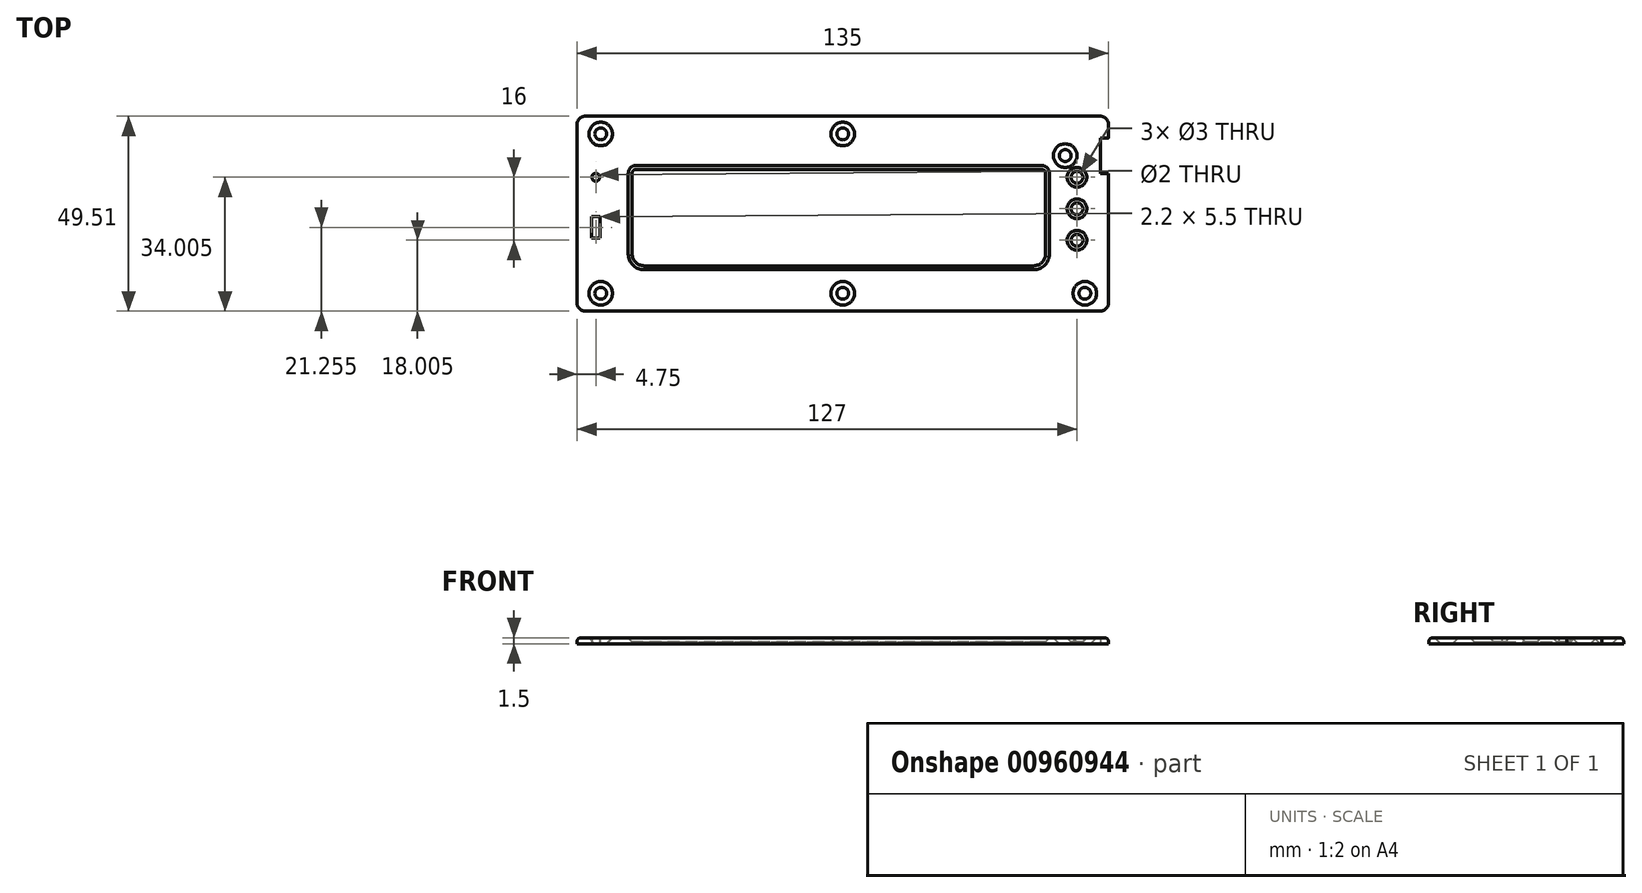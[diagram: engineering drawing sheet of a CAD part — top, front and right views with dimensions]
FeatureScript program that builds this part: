
annotation { "Feature Type Name" : "Feature", "Feature Type Description" : "" }
export const myFeature = defineFeature(function(context is Context, id is Id, definition is map)
    precondition{}
    {
        {
            var Q0;
            Q0=qCreatedBy(makeId("Top.planeOp"),FACE);
            var sketch = newSketch(context, id + "F0", { "sketchPlane" : qUnion([Q0])});
            skLineSegment(sketch, "E0.bottom", {"start": v(70.6, 17.07) * mm, "end": v(-60.4, 17.07) * mm});
            skLineSegment(sketch, "E0.top", {"start": v(70.6, -21.43) * mm, "end": v(-60.4, -21.43) * mm});
            skLineSegment(sketch, "E0.left", {"start": v(70.6, 17.07) * mm, "end": v(70.6, -21.43) * mm});
            skLineSegment(sketch, "E0.right", {"start": v(-60.4, 17.07) * mm, "end": v(-60.4, -21.43) * mm});
            skPoint(sketch, "E1", {"position": v(54.1, 17.07) * mm});
            skPoint(sketch, "E2", {"position": v(-60.4, 8.07) * mm});
            skLineSegment(sketch, "E3", {"start": v(-60.4, 8.07) * mm, "end": v(54.1, 8.08) * mm});
            skLineSegment(sketch, "E4", {"start": v(54.1, 8.08) * mm, "end": v(54.1, 17.07) * mm});
            skPoint(sketch, "E5", {"position": v(-54.9, -21.43) * mm});
            skLineSegment(sketch, "E6", {"start": v(-54.9, -21.43) * mm, "end": v(-54.9, 8.07) * mm});
            skLineSegment(sketch, "E7.0", {"start": v(72.6, 19.08) * mm, "end": v(-62.4, 19.08) * mm});
            skLineSegment(sketch, "E7.1", {"start": v(72.6, 19.08) * mm, "end": v(72.6, -23.43) * mm});
            skLineSegment(sketch, "E7.2", {"start": v(72.6, -23.43) * mm, "end": v(-62.4, -23.43) * mm});
            skLineSegment(sketch, "E7.3", {"start": v(-62.4, 19.08) * mm, "end": v(-62.4, -23.43) * mm});
            skPoint(sketch, "E8", {"position": v(70.6, 13.58) * mm});
            skPoint(sketch, "E9", {"position": v(70.6, 4.57) * mm});
            skLineSegment(sketch, "E10.0", {"start": v(52.1, 10.08) * mm, "end": v(52.1, 17.07) * mm});
            skLineSegment(sketch, "E10.1", {"start": v(-60.4, 10.07) * mm, "end": v(52.1, 10.08) * mm});
            skPoint(sketch, "E11", {"position": v(-60.4, -0.93) * mm});
            skLineSegment(sketch, "E12", {"start": v(-60.4, -0.93) * mm, "end": v(-54.9, -0.93) * mm});
            skLineSegment(sketch, "E13.0", {"start": v(-60.4, -2.93) * mm, "end": v(-54.9, -2.93) * mm});
            skLineSegment(sketch, "E14", {"start": v(52.1, 17.07) * mm, "end": v(52.1, 19.08) * mm});
            skLineSegment(sketch, "E15", {"start": v(-60.4, 10.07) * mm, "end": v(-62.4, 10.07) * mm});
            skLineSegment(sketch, "E16", {"start": v(-60.4, 8.07) * mm, "end": v(-62.4, 8.07) * mm});
            skLineSegment(sketch, "E17", {"start": v(-60.4, -0.93) * mm, "end": v(-62.4, -0.93) * mm});
            skLineSegment(sketch, "E18", {"start": v(-60.4, -2.93) * mm, "end": v(-62.4, -2.93) * mm});
            skLineSegment(sketch, "E19", {"start": v(70.6, 13.58) * mm, "end": v(72.6, 13.58) * mm});
            skLineSegment(sketch, "E20", {"start": v(70.6, 4.57) * mm, "end": v(72.6, 4.57) * mm});
            skPoint(sketch, "E21", {"position": v(-49.9, -21.43) * mm});
            skPoint(sketch, "E22", {"position": v(56.6, -21.42) * mm});
            skLineSegment(sketch, "E23", {"start": v(56.6, -15.93) * mm, "end": v(56.6, 4.57) * mm});
            skPoint(sketch, "E23.endSnap0", {"position": v(-3.15, 8.08) * mm});
            skPoint(sketch, "E24", {"position": v(-49.9, 5.58) * mm});
            skLineSegment(sketch, "E25", {"start": v(-47.4, 5.58) * mm, "end": v(55.6, 5.57) * mm});
            skPoint(sketch, "E26.newPointA", {"position": v(56.6, 8.08) * mm});
            skArc(sketch, "E26.filletArc", {"start": v(56.6, 4.57) * mm, "mid": v(56.3, 5.28) * mm, "end": v(55.6, 5.57) * mm});
            skPoint(sketch, "E27.visualSharp", {"position": v(-49.9, -18.93) * mm});
            skPoint(sketch, "E28.visualSharp", {"position": v(56.6, -18.93) * mm});
            skArc(sketch, "E28.filletArc", {"start": v(53.6, -18.93) * mm, "mid": v(55.72, -18.05) * mm, "end": v(56.6, -15.93) * mm});
            skPoint(sketch, "E29", {"position": v(-57.65, -2.93) * mm});
            skPoint(sketch, "E30", {"position": v(-58.75, -2.93) * mm});
            skPoint(sketch, "E31", {"position": v(-56.55, -2.93) * mm});
            skLineSegment(sketch, "E32", {"start": v(-58.75, -2.93) * mm, "end": v(-58.75, -21.43) * mm});
            skLineSegment(sketch, "E33", {"start": v(-56.55, -2.93) * mm, "end": v(-56.55, -21.43) * mm});
            skPoint(sketch, "E34", {"position": v(-56.55, -10.43) * mm});
            skPoint(sketch, "E35", {"position": v(-56.55, -7.93) * mm});
            skPoint(sketch, "E36", {"position": v(-56.55, -11.93) * mm});
            skPoint(sketch, "E37", {"position": v(-56.55, -6.43) * mm});
            skLineSegment(sketch, "E38.bottom", {"start": v(-56.55, -11.93) * mm, "end": v(-58.75, -11.93) * mm});
            skLineSegment(sketch, "E38.top", {"start": v(-56.55, -6.43) * mm, "end": v(-58.75, -6.43) * mm});
            skLineSegment(sketch, "E38.left", {"start": v(-56.55, -11.93) * mm, "end": v(-56.55, -6.43) * mm});
            skLineSegment(sketch, "E38.right", {"start": v(-58.75, -11.93) * mm, "end": v(-58.75, -6.43) * mm});
            skLineSegment(sketch, "E39.bottom", {"start": v(-62.4, -23.43) * mm, "end": v(72.6, -23.43) * mm});
            skLineSegment(sketch, "E39.top", {"start": v(-62.4, -30.42) * mm, "end": v(72.6, -30.42) * mm});
            skLineSegment(sketch, "E39.left", {"start": v(-62.4, -23.43) * mm, "end": v(-62.4, -30.42) * mm});
            skLineSegment(sketch, "E39.right", {"start": v(72.6, -23.43) * mm, "end": v(72.6, -30.42) * mm});
            skPoint(sketch, "E40", {"position": v(72.6, -25.92) * mm});
            skLineSegment(sketch, "E41", {"start": v(72.6, -25.92) * mm, "end": v(-62.4, -25.92) * mm, "construction": true});
            skPoint(sketch, "E42", {"position": v(5.1, -25.93) * mm});
            skPoint(sketch, "E43", {"position": v(66.6, -25.93) * mm});
            skPoint(sketch, "E44", {"position": v(-56.4, -25.93) * mm});
            skCircle(sketch, "E45", {"center": v(-56.4, -25.93) * mm, "radius": 1.5 * mm});
            skCircle(sketch, "E46", {"center": v(5.1, -25.93) * mm, "radius": 1.5 * mm});
            skCircle(sketch, "E47", {"center": v(66.6, -25.93) * mm, "radius": 1.5 * mm});
            skPoint(sketch, "E48", {"position": v(-62.4, 14.58) * mm});
            skLineSegment(sketch, "E49", {"start": v(-62.4, 14.58) * mm, "end": v(72.6, 14.57) * mm, "construction": true});
            skPoint(sketch, "E50", {"position": v(-56.4, 14.58) * mm});
            skPoint(sketch, "E51", {"position": v(5.1, 14.58) * mm});
            skCircle(sketch, "E52", {"center": v(-56.4, 14.58) * mm, "radius": 1.5 * mm});
            skCircle(sketch, "E53", {"center": v(5.1, 14.58) * mm, "radius": 1.5 * mm});
            skPoint(sketch, "E54", {"position": v(70.6, 9.08) * mm});
            skPoint(sketch, "E55", {"position": v(61.6, 9.08) * mm});
            skCircle(sketch, "E56", {"center": v(61.6, 9.08) * mm, "radius": 1.5 * mm});
            skPoint(sketch, "E57", {"position": v(67.56, -30.42) * mm});
            skLineSegment(sketch, "E58", {"start": v(66.6, -25.93) * mm, "end": v(66.6, 14.57) * mm, "construction": true});
            skPoint(sketch, "E59", {"position": v(66.6, -12.42) * mm});
            skPoint(sketch, "E60", {"position": v(66.6, -4.42) * mm});
            skPoint(sketch, "E61", {"position": v(66.6, 3.58) * mm});
            skPoint(sketch, "E62", {"position": v(-48.4, 5.57) * mm});
            skLineSegment(sketch, "E63", {"start": v(-48.4, 4.58) * mm, "end": v(-48.4, -15.93) * mm});
            skPoint(sketch, "E64.visualSharp", {"position": v(-48.4, 5.58) * mm});
            skArc(sketch, "E64.filletArc", {"start": v(-47.4, 5.58) * mm, "mid": v(-48.1, 5.28) * mm, "end": v(-48.4, 4.58) * mm});
            skLineSegment(sketch, "E65", {"start": v(-45.4, -18.93) * mm, "end": v(53.6, -18.93) * mm});
            skPoint(sketch, "E66.visualSharp", {"position": v(-48.4, -18.93) * mm});
            skArc(sketch, "E66.filletArc", {"start": v(-48.4, -15.93) * mm, "mid": v(-47.52, -18.05) * mm, "end": v(-45.4, -18.93) * mm});
            skPoint(sketch, "E67", {"position": v(64.6, 3.58) * mm});
            skPoint(sketch, "E68", {"position": v(64.6, -4.42) * mm});
            skPoint(sketch, "E69", {"position": v(64.6, -12.42) * mm});
            skCircle(sketch, "E70", {"center": v(64.6, 3.58) * mm, "radius": 1.5 * mm});
            skCircle(sketch, "E71", {"center": v(64.6, -4.42) * mm, "radius": 1.5 * mm});
            skCircle(sketch, "E72", {"center": v(64.6, -12.42) * mm, "radius": 1.5 * mm});
            skPoint(sketch, "E73", {"position": v(-57.65, 8.08) * mm});
            skPoint(sketch, "E74", {"position": v(-60.4, 3.58) * mm});
            skPoint(sketch, "E75", {"position": v(-57.65, 3.58) * mm});
            skCircle(sketch, "E76", {"center": v(-57.65, 3.58) * mm, "radius": 1 * mm});
            skSolve(sketch);
        }
        {
            var Q0;
            {var subQ4=sQuery(id+"F0.wireOp",EDGE,"E4");Q0=makeQuery(id+"F0.imprint","IMPRINT",FACE,{"disambiguationData":[TD([[makeQuery(id+"F0.imprint","IMPRINT",EDGE,{"derivedFrom":subQ4}),1.0]])]});}
            var Q1;
            {var subQ4=sQuery(id+"F0.wireOp",EDGE,"E14");Q1=makeQuery(id+"F0.imprint","IMPRINT",FACE,{"disambiguationData":[TD([[makeQuery(id+"F0.imprint","IMPRINT",EDGE,{"derivedFrom":subQ4}),1.0]])]});}
            var Q2;
            {var subQ1=sQuery(id+"F0.wireOp",EDGE,"E10.0");Q2=makeQuery(id+"F0.imprint","IMPRINT",FACE,{"disambiguationData":[TD([[makeQuery(id+"F0.imprint","IMPRINT",EDGE,{"derivedFrom":subQ1}),1.0]])]});}
            var Q3;
            {var subQ4=sQuery(id+"F0.wireOp",EDGE,"E14");Q3=makeQuery(id+"F0.imprint","IMPRINT",FACE,{"disambiguationData":[TD([[makeQuery(id+"F0.imprint","IMPRINT",EDGE,{"derivedFrom":subQ4}),-1.0]])]});}
            var Q4;
            {var subQ0=sQuery(id+"F0.wireOp",EDGE,"E4");Q4=makeQuery(id+"F0.imprint","IMPRINT",FACE,{"disambiguationData":[TD([[makeQuery(id+"F0.imprint","IMPRINT",EDGE,{"derivedFrom":subQ0}),-1.0]])]});}
            var Q5;
            {var subQ3=sQuery(id+"F0.wireOp",EDGE,"E7.2");Q5=makeQuery(id+"F0.imprint","IMPRINT",FACE,{"disambiguationData":[TD([[makeQuery(id+"F0.imprint","IMPRINT",EDGE,{"derivedFrom":subQ3}),-1.0]])]});}
            var Q6;
            Q6=makeQuery(id+"F0.imprint","IMPRINT",FACE,{"disambiguationData":[TD([[makeQuery(id+"F0.imprint","IMPRINT",EDGE,{"derivedFrom":sQuery(id+"F0.wireOp",EDGE,"E7.2")}),1.0]])]});
            var Q7;
            {var subQ2=sQuery(id+"F0.wireOp",EDGE,"E15");Q7=makeQuery(id+"F0.imprint","IMPRINT",FACE,{"disambiguationData":[TD([[makeQuery(id+"F0.imprint","IMPRINT",EDGE,{"derivedFrom":subQ2}),1.0]])]});}
            var Q8;
            {var subQ0=sQuery(id+"F0.wireOp",EDGE,"E16");Q8=makeQuery(id+"F0.imprint","IMPRINT",FACE,{"disambiguationData":[TD([[makeQuery(id+"F0.imprint","IMPRINT",EDGE,{"derivedFrom":subQ0}),1.0]])]});}
            var Q9;
            {var subQ2=sQuery(id+"F0.wireOp",EDGE,"E17");Q9=makeQuery(id+"F0.imprint","IMPRINT",FACE,{"disambiguationData":[TD([[makeQuery(id+"F0.imprint","IMPRINT",EDGE,{"derivedFrom":subQ2}),1.0]])]});}
            var Q10;
            {var subQ0=sQuery(id+"F0.wireOp",EDGE,"E12");Q10=makeQuery(id+"F0.imprint","IMPRINT",FACE,{"disambiguationData":[TD([[makeQuery(id+"F0.imprint","IMPRINT",EDGE,{"derivedFrom":subQ0}),1.0]])]});}
            var Q11;
            {var subQ0=sQuery(id+"F0.wireOp",EDGE,"E12");Q11=makeQuery(id+"F0.imprint","IMPRINT",FACE,{"disambiguationData":[TD([[makeQuery(id+"F0.imprint","IMPRINT",EDGE,{"derivedFrom":subQ0}),-1.0]])]});}
            var Q12;
            {var subQ5=sQuery(id+"F0.wireOp",EDGE,"E38.top");Q12=makeQuery(id+"F0.imprint","IMPRINT",FACE,{"disambiguationData":[TD([[makeQuery(id+"F0.imprint","IMPRINT",EDGE,{"derivedFrom":subQ5}),-1.0]])]});}
            var Q13;
            {var subQ2=sQuery(id+"F0.wireOp",EDGE,"E0.top");var subQ5=sQuery(id+"F0.wireOp",EDGE,"E6");var subQ8=makeQuery(id+"F0.imprint","INTERSECT",VERTEX,{"derivedFrom":[subQ2,subQ5]});Q13=makeQuery(id+"F0.imprint","IMPRINT",FACE,{"disambiguationData":[TD([[makeQuery(id+"F0.imprint","IMPRINT",EDGE,{"disambiguationData":[TD([[subQ8,-1.0]])],"derivedFrom":subQ2}),-1.0]])]});}
            var Q14;
            {var subQ2=sQuery(id+"F0.wireOp",EDGE,"E0.top");var subQ5=sQuery(id+"F0.wireOp",EDGE,"E0.right");var subQ8=makeQuery(id+"F0.imprint","INTERSECT",VERTEX,{"derivedFrom":[subQ2,subQ5]});Q14=makeQuery(id+"F0.imprint","IMPRINT",FACE,{"disambiguationData":[TD([[makeQuery(id+"F0.imprint","IMPRINT",EDGE,{"disambiguationData":[TD([[subQ8,1.0]])],"derivedFrom":subQ2}),-1.0]])]});}
            var Q15;
            {var subQ5=sQuery(id+"F0.wireOp",EDGE,"E38.bottom");Q15=makeQuery(id+"F0.imprint","IMPRINT",FACE,{"disambiguationData":[TD([[makeQuery(id+"F0.imprint","IMPRINT",EDGE,{"derivedFrom":subQ5}),1.0]])]});}
            extrude(context, id + "F1", {"entities" : qUnion([Q0, Q1, Q2, Q3, Q4, Q5, Q6, Q7, Q8, Q9, Q10, Q11, Q12, Q13, Q14, Q15]), "depth" : 1.5 * mm, "offsetDistance" : 25 * mm});
        }
        {
            var Q0;
            Q0=makeQuery(id+"F1.opExtrude","CAP_EDGE",EDGE,{"disambiguationData":[OSD([sQuery(id+"F0.wireOp",EDGE,"E7.3"),sQuery(id+"F0.wireOp",EDGE,"E39.left")])],"isStart":false});
            var Q1;
            Q1=makeQuery(id+"F1.opExtrude","CAP_EDGE",EDGE,{"disambiguationData":[OSD([sQuery(id+"F0.wireOp",EDGE,"E7.0")])],"isStart":false});
            var Q2;
            Q2=makeQuery(id+"F1.opExtrude","CAP_EDGE",EDGE,{"disambiguationData":[OSD([sQuery(id+"F0.wireOp",EDGE,"E7.1")])],"isStart":false});
            var Q3;
            Q3=makeQuery(id+"F1.opExtrude","CAP_EDGE",EDGE,{"disambiguationData":[OSD([sQuery(id+"F0.wireOp",EDGE,"E7.1"),sQuery(id+"F0.wireOp",EDGE,"E39.right")])],"isStart":false});
            var Q4;
            Q4=makeQuery(id+"F1.opExtrude","CAP_EDGE",EDGE,{"disambiguationData":[OSD([sQuery(id+"F0.wireOp",EDGE,"E39.top")])],"isStart":false});
            fillet(context, id + "F2", {"entities" : qUnion([Q0, Q1, Q2, Q3, Q4]), "radius" : 1 * mm, "tangentPropagation" : true, "allowEdgeOverflow" : false});
        }
        {
            var Q0;
            Q0=makeQuery(id+"F1.opExtrude","SWEPT_EDGE",EDGE,{"disambiguationData":[OSD([sQuery(id+"F0.wireOp",EDGE,"E7.0"),sQuery(id+"F0.wireOp",EDGE,"E7.3")])]});
            var Q1;
            Q1=makeQuery(id+"F1.opExtrude","SWEPT_EDGE",EDGE,{"disambiguationData":[OSD([sQuery(id+"F0.wireOp",EDGE,"E7.0"),sQuery(id+"F0.wireOp",EDGE,"E7.1")])]});
            var Q2;
            Q2=makeQuery(id+"F1.opExtrude","SWEPT_EDGE",EDGE,{"disambiguationData":[OSD([sQuery(id+"F0.wireOp",EDGE,"E39.top"),sQuery(id+"F0.wireOp",EDGE,"E39.right")])]});
            var Q3;
            Q3=makeQuery(id+"F1.opExtrude","SWEPT_EDGE",EDGE,{"disambiguationData":[OSD([sQuery(id+"F0.wireOp",EDGE,"E39.top"),sQuery(id+"F0.wireOp",EDGE,"E39.left")])]});
            fillet(context, id + "F3", {"entities" : qUnion([Q0, Q1, Q2, Q3]), "radius" : 2 * mm, "tangentPropagation" : true, "allowEdgeOverflow" : false});
        }
        {
            var Q0;
            Q0=makeQuery(id+"F1.opExtrude","CAP_EDGE",EDGE,{"disambiguationData":[OSD([sQuery(id+"F0.wireOp",EDGE,"111bff33-9754-4fc8-a8c8-71f33a6abdcf.filletArc")])],"isStart":false});
            var Q1;
            Q1=makeQuery(id+"F1.opExtrude","CAP_EDGE",EDGE,{"disambiguationData":[OSD([sQuery(id+"F0.wireOp",EDGE,"E25")])],"isStart":false});
            var Q2;
            Q2=makeQuery(id+"F1.opExtrude","CAP_EDGE",EDGE,{"disambiguationData":[OSD([sQuery(id+"F0.wireOp",EDGE,"g5umVIkw-vWO4-hGJM-yZ5A-3RqCPJ1O2B3R")])],"isStart":false});
            var Q3;
            Q3=makeQuery(id+"F1.opExtrude","CAP_EDGE",EDGE,{"disambiguationData":[OSD([sQuery(id+"F0.wireOp",EDGE,"E27.filletArc")])],"isStart":false});
            var Q4;
            Q4=makeQuery(id+"F1.opExtrude","CAP_EDGE",EDGE,{"disambiguationData":[OSD([sQuery(id+"F0.wireOp",EDGE,"1fmAiX83-1eq4-HNST-ceWr-fLASINAnwhCB")])],"isStart":false});
            var Q5;
            Q5=makeQuery(id+"F1.opExtrude","CAP_EDGE",EDGE,{"disambiguationData":[OSD([sQuery(id+"F0.wireOp",EDGE,"E28.filletArc")])],"isStart":false});
            var Q6;
            Q6=makeQuery(id+"F1.opExtrude","CAP_EDGE",EDGE,{"disambiguationData":[OSD([sQuery(id+"F0.wireOp",EDGE,"E23")])],"isStart":false});
            var Q7;
            Q7=makeQuery(id+"F1.opExtrude","CAP_EDGE",EDGE,{"disambiguationData":[OSD([sQuery(id+"F0.wireOp",EDGE,"E26.filletArc")])],"isStart":false});
            chamfer(context, id + "F4", {"entities" : qUnion([Q0, Q1, Q2, Q3, Q4, Q5, Q6, Q7]), "width" : 1 * mm, "tangentPropagation" : true});
        }
        {
            var Q0;
            Q0=makeQuery(id+"F1.opExtrude","CAP_EDGE",EDGE,{"disambiguationData":[OSD([sQuery(id+"F0.wireOp",EDGE,"E70")])],"isStart":false});
            var Q1;
            Q1=makeQuery(id+"F1.opExtrude","CAP_EDGE",EDGE,{"disambiguationData":[OSD([sQuery(id+"F0.wireOp",EDGE,"E71")])],"isStart":false});
            var Q2;
            Q2=makeQuery(id+"F1.opExtrude","CAP_EDGE",EDGE,{"disambiguationData":[OSD([sQuery(id+"F0.wireOp",EDGE,"E72")])],"isStart":false});
            chamfer(context, id + "F5", {"entities" : qUnion([Q0, Q1, Q2]), "width" : 1 * mm, "tangentPropagation" : true});
        }
        {
            var Q0;
            Q0=makeQuery(id+"F1.opExtrude","CAP_EDGE",EDGE,{"disambiguationData":[OSD([sQuery(id+"F0.wireOp",EDGE,"E53")])],"isStart":false});
            var Q1;
            Q1=makeQuery(id+"F1.opExtrude","CAP_EDGE",EDGE,{"disambiguationData":[OSD([sQuery(id+"F0.wireOp",EDGE,"E56")])],"isStart":false});
            var Q2;
            Q2=makeQuery(id+"F1.opExtrude","CAP_EDGE",EDGE,{"disambiguationData":[OSD([sQuery(id+"F0.wireOp",EDGE,"E47")])],"isStart":false});
            var Q3;
            Q3=makeQuery(id+"F1.opExtrude","CAP_EDGE",EDGE,{"disambiguationData":[OSD([sQuery(id+"F0.wireOp",EDGE,"E46")])],"isStart":false});
            var Q4;
            Q4=makeQuery(id+"F1.opExtrude","CAP_EDGE",EDGE,{"disambiguationData":[OSD([sQuery(id+"F0.wireOp",EDGE,"E45")])],"isStart":false});
            var Q5;
            Q5=makeQuery(id+"F1.opExtrude","CAP_EDGE",EDGE,{"disambiguationData":[OSD([sQuery(id+"F0.wireOp",EDGE,"E52")])],"isStart":false});
            chamfer(context, id + "F6", {"entities" : qUnion([Q0, Q1, Q2, Q3, Q4, Q5]), "width" : 1.5 * mm, "tangentPropagation" : true});
        }
    });
